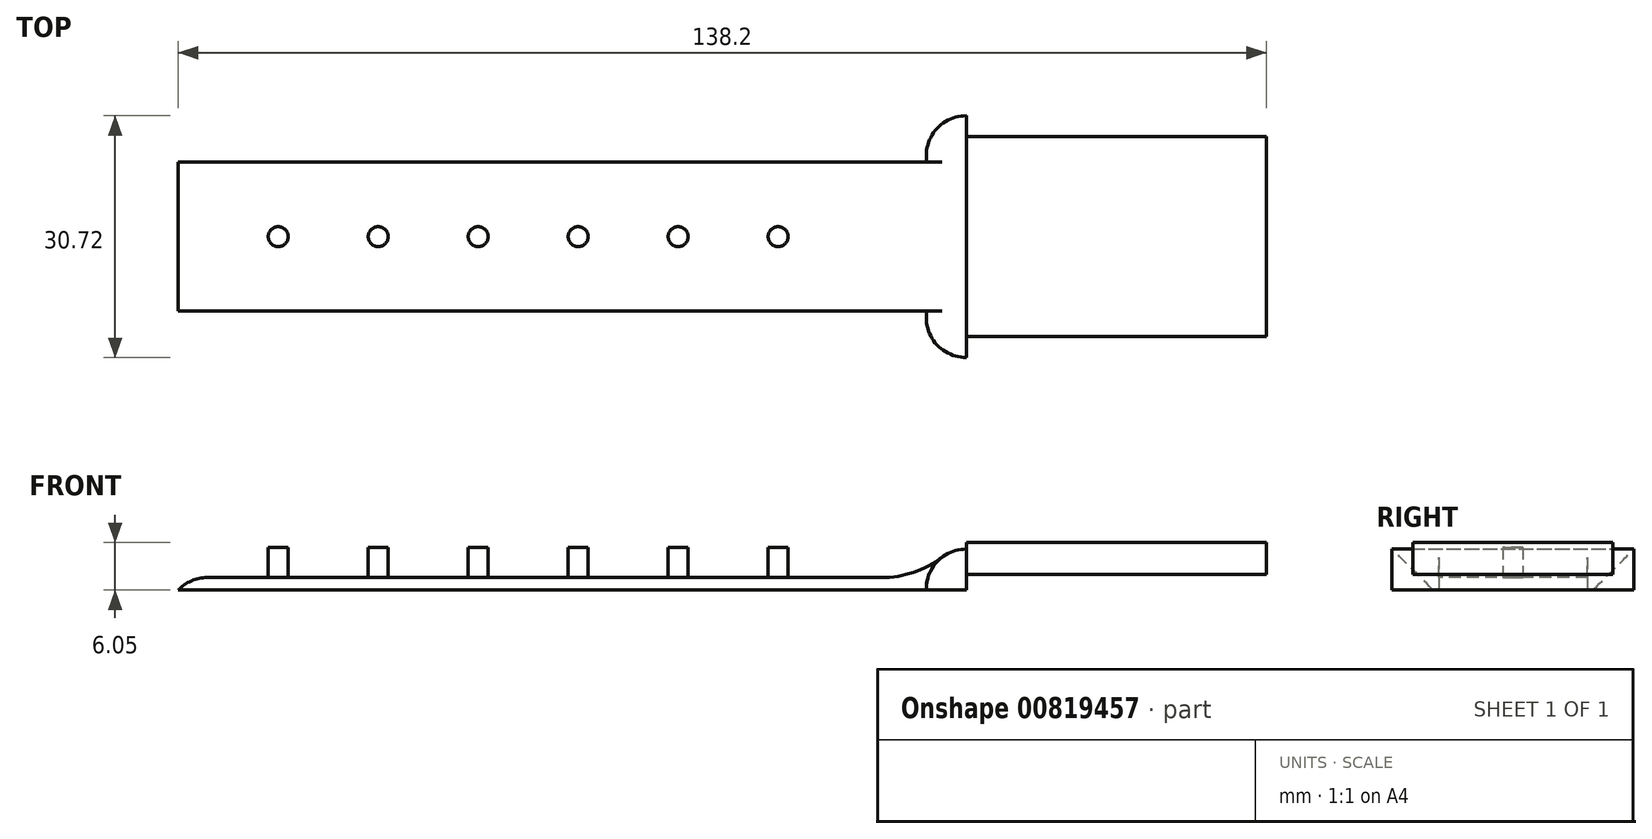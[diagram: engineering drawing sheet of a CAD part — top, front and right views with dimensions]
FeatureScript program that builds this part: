
annotation { "Feature Type Name" : "Feature", "Feature Type Description" : "" }
export const myFeature = defineFeature(function(context is Context, id is Id, definition is map)
    precondition{}
    {
        {
            var Q0;
            Q0=qCreatedBy(makeId("Top.planeOp"),FACE);
            var sketch = newSketch(context, id + "F0", { "sketchPlane" : qUnion([Q0])});
            skLineSegment(sketch, "E0.bottom", {"start": v(24.46, -15.36) * mm, "end": v(-24.46, -15.36) * mm});
            skLineSegment(sketch, "E0.top", {"start": v(24.46, 15.36) * mm, "end": v(-24.46, 15.36) * mm});
            skLineSegment(sketch, "E0.left", {"start": v(24.46, -15.36) * mm, "end": v(24.46, 15.36) * mm});
            skLineSegment(sketch, "E0.right", {"start": v(-24.46, -15.36) * mm, "end": v(-24.46, 15.36) * mm});
            skPoint(sketch, "E0.middle", {"position": v(0, 0) * mm});
            skLineSegment(sketch, "E1.bottom", {"start": v(-24.46, -9.45) * mm, "end": v(-119.48, -9.45) * mm});
            skLineSegment(sketch, "E1.top", {"start": v(-24.46, 9.45) * mm, "end": v(-119.48, 9.45) * mm});
            skLineSegment(sketch, "E1.left", {"start": v(-24.46, -9.45) * mm, "end": v(-24.46, 9.45) * mm});
            skLineSegment(sketch, "E1.right", {"start": v(-119.48, -9.45) * mm, "end": v(-119.48, 9.45) * mm});
            skLineSegment(sketch, "E2.MirrorCS", {"start": v(24.46, 9.45) * mm, "end": v(119.48, 9.45) * mm});
            skLineSegment(sketch, "E3.MirrorCS", {"start": v(119.48, -9.45) * mm, "end": v(119.48, 9.45) * mm});
            skLineSegment(sketch, "E4.MirrorCS", {"start": v(24.46, -9.45) * mm, "end": v(119.48, -9.45) * mm});
            skSolve(sketch);
        }
        {
            var Q0;
            Q0=qSketchRegion(id+"F0",true);
            extrude(context, id + "F1", {"entities" : qUnion([Q0]), "depth" : 1.6 * mm, "offsetDistance" : 25.4 * mm});
        }
        {
            var Q0;
            Q0=makeQuery(id+"F1.opExtrude","CAP_FACE",FACE,{"disambiguationData":[OSD([sQuery(id+"F0.wireOp",EDGE,"E0.bottom"),sQuery(id+"F0.wireOp",EDGE,"E0.top"),sQuery(id+"F0.wireOp",EDGE,"E0.left"),sQuery(id+"F0.wireOp",EDGE,"E0.right"),sQuery(id+"F0.wireOp",EDGE,"E1.bottom"),sQuery(id+"F0.wireOp",EDGE,"E1.top"),sQuery(id+"F0.wireOp",EDGE,"E1.right"),sQuery(id+"F0.wireOp",EDGE,"E2.MirrorCS"),sQuery(id+"F0.wireOp",EDGE,"E3.MirrorCS"),sQuery(id+"F0.wireOp",EDGE,"E4.MirrorCS")])],"isStart":false});
            var sketch = newSketch(context, id + "F2", { "sketchPlane" : qUnion([Q0])});
            skLineSegment(sketch, "E5", {"start": v(119.48, 0) * mm, "end": v(106.78, 0) * mm, "construction": true});
            skLineSegment(sketch, "E6", {"start": v(106.78, 0) * mm, "end": v(94.08, 0) * mm, "construction": true});
            skLineSegment(sketch, "E7", {"start": v(94.08, 0) * mm, "end": v(81.38, 0) * mm, "construction": true});
            skLineSegment(sketch, "E8", {"start": v(81.38, 0) * mm, "end": v(68.68, 0) * mm, "construction": true});
            skLineSegment(sketch, "E9", {"start": v(68.68, 0) * mm, "end": v(55.98, 0) * mm, "construction": true});
            skLineSegment(sketch, "E10", {"start": v(55.98, 0) * mm, "end": v(43.28, 0) * mm, "construction": true});
            skCircle(sketch, "E11", {"center": v(106.78, 0) * mm, "radius": 1.27 * mm});
            skCircle(sketch, "E12", {"center": v(94.08, 0) * mm, "radius": 1.27 * mm});
            skCircle(sketch, "E13", {"center": v(81.38, 0) * mm, "radius": 1.27 * mm});
            skCircle(sketch, "E14", {"center": v(68.68, 0) * mm, "radius": 1.27 * mm});
            skCircle(sketch, "E15", {"center": v(55.98, 0) * mm, "radius": 1.27 * mm});
            skCircle(sketch, "E16", {"center": v(43.28, 0) * mm, "radius": 1.27 * mm});
            skSolve(sketch);
        }
        {
            var Q0;
            Q0=qSketchRegion(id+"F2",true);
            extrude(context, id + "F3", {"entities" : qUnion([Q0]), "operationType" : NewBodyOperationType.REMOVE, "oppositeDirection" : true, "depth" : 25.4 * mm, "offsetDistance" : 25.4 * mm});
        }
        {
            var Q0;
            Q0=makeQuery(id+"F2.imprint","IMPRINT",FACE,{"disambiguationData":[TD([[makeQuery(id+"F2.imprint","IMPRINT",EDGE,{"derivedFrom":sQuery(id+"F2.wireOp",EDGE,"E11")}),-1.0]])]});
            var sketch = newSketch(context, id + "F4", { "sketchPlane" : qUnion([Q0])});
            skLineSegment(sketch, "E17", {"start": v(-119.47, 0) * mm, "end": v(-106.77, 0) * mm, "construction": true});
            skLineSegment(sketch, "E18", {"start": v(-106.77, 0) * mm, "end": v(-94.07, 0) * mm, "construction": true});
            skLineSegment(sketch, "E19", {"start": v(-94.07, 0) * mm, "end": v(-81.37, 0) * mm, "construction": true});
            skLineSegment(sketch, "E20", {"start": v(-81.37, 0) * mm, "end": v(-68.67, 0) * mm, "construction": true});
            skLineSegment(sketch, "E21", {"start": v(-68.67, 0) * mm, "end": v(-55.97, 0) * mm, "construction": true});
            skLineSegment(sketch, "E22", {"start": v(-55.97, 0) * mm, "end": v(-43.27, 0) * mm, "construction": true});
            skCircle(sketch, "E23", {"center": v(-106.77, 0) * mm, "radius": 1.27 * mm});
            skCircle(sketch, "E24", {"center": v(-94.07, 0) * mm, "radius": 1.27 * mm});
            skCircle(sketch, "E25", {"center": v(-81.37, 0) * mm, "radius": 1.27 * mm});
            skCircle(sketch, "E26", {"center": v(-68.67, 0) * mm, "radius": 1.27 * mm});
            skCircle(sketch, "E27", {"center": v(-55.97, 0) * mm, "radius": 1.27 * mm});
            skCircle(sketch, "E28", {"center": v(-43.27, 0) * mm, "radius": 1.27 * mm});
            skSolve(sketch);
        }
        {
            var Q0;
            Q0=qSketchRegion(id+"F4",true);
            extrude(context, id + "F5", {"entities" : qUnion([Q0]), "operationType" : NewBodyOperationType.ADD, "depth" : 3.8 * mm, "offsetDistance" : 25.4 * mm});
        }
        {
            var Q0;
            Q0=makeQuery(id+"F1.opExtrude","CAP_FACE",FACE,{"disambiguationData":[OSD([sQuery(id+"F0.wireOp",EDGE,"E0.bottom"),sQuery(id+"F0.wireOp",EDGE,"E0.top"),sQuery(id+"F0.wireOp",EDGE,"E0.left"),sQuery(id+"F0.wireOp",EDGE,"E0.right"),sQuery(id+"F0.wireOp",EDGE,"E1.bottom"),sQuery(id+"F0.wireOp",EDGE,"E1.top"),sQuery(id+"F0.wireOp",EDGE,"E1.right"),sQuery(id+"F0.wireOp",EDGE,"E2.MirrorCS"),sQuery(id+"F0.wireOp",EDGE,"E3.MirrorCS"),sQuery(id+"F0.wireOp",EDGE,"E4.MirrorCS")])],"isStart":false});
            var sketch = newSketch(context, id + "F6", { "sketchPlane" : qUnion([Q0])});
            skLineSegment(sketch, "E29.bottom", {"start": v(-24.46, 15.36) * mm, "end": v(24.46, 15.36) * mm});
            skLineSegment(sketch, "E29.top", {"start": v(-24.46, -15.36) * mm, "end": v(24.46, -15.36) * mm});
            skLineSegment(sketch, "E29.left", {"start": v(-24.46, 15.36) * mm, "end": v(-24.46, -15.36) * mm});
            skLineSegment(sketch, "E29.right", {"start": v(24.46, 15.36) * mm, "end": v(24.46, -15.36) * mm});
            skSolve(sketch);
        }
        {
            var Q0;
            Q0=qSketchRegion(id+"F6",true);
            extrude(context, id + "F7", {"entities" : qUnion([Q0]), "operationType" : NewBodyOperationType.ADD, "depth" : 3.62 * mm, "offsetDistance" : 25.4 * mm});
        }
        {
            var Q0;
            Q0=makeQuery(id+"F7.opExtrude","CAP_EDGE",EDGE,{"disambiguationData":[OSD([sQuery(id+"F6.wireOp",EDGE,"E29.right")])],"isStart":false});
            var Q1;
            Q1=makeQuery(id+"F7.opExtrude","CAP_EDGE",EDGE,{"disambiguationData":[OSD([sQuery(id+"F6.wireOp",EDGE,"E29.left")])],"isStart":false});
            var Q2;
            Q2=makeQuery(id+"F7.boolean.opBoolean","MERGE",EDGE,{"derivedFrom":[makeQuery(id+"F1.opExtrude","SWEPT_EDGE",EDGE,{"disambiguationData":[OSD([sQuery(id+"F0.wireOp",EDGE,"E0.top"),sQuery(id+"F0.wireOp",EDGE,"E0.right")])]}),makeQuery(id+"F7.opExtrude","SWEPT_EDGE",EDGE,{"disambiguationData":[OSD([sQuery(id+"F6.wireOp",EDGE,"E29.bottom"),sQuery(id+"F6.wireOp",EDGE,"E29.left")])]})]});
            var Q3;
            Q3=makeQuery(id+"F7.boolean.opBoolean","MERGE",EDGE,{"derivedFrom":[makeQuery(id+"F1.opExtrude","SWEPT_EDGE",EDGE,{"disambiguationData":[OSD([sQuery(id+"F0.wireOp",EDGE,"E0.bottom"),sQuery(id+"F0.wireOp",EDGE,"E0.right")])]}),makeQuery(id+"F7.opExtrude","SWEPT_EDGE",EDGE,{"disambiguationData":[OSD([sQuery(id+"F6.wireOp",EDGE,"E29.top"),sQuery(id+"F6.wireOp",EDGE,"E29.left")])]})]});
            var Q4;
            Q4=makeQuery(id+"F7.boolean.opBoolean","MERGE",EDGE,{"derivedFrom":[makeQuery(id+"F1.opExtrude","SWEPT_EDGE",EDGE,{"disambiguationData":[OSD([sQuery(id+"F0.wireOp",EDGE,"E0.bottom"),sQuery(id+"F0.wireOp",EDGE,"E0.left")])]}),makeQuery(id+"F7.opExtrude","SWEPT_EDGE",EDGE,{"disambiguationData":[OSD([sQuery(id+"F6.wireOp",EDGE,"E29.top"),sQuery(id+"F6.wireOp",EDGE,"E29.right")])]})]});
            var Q5;
            Q5=makeQuery(id+"F7.boolean.opBoolean","MERGE",EDGE,{"derivedFrom":[makeQuery(id+"F1.opExtrude","SWEPT_EDGE",EDGE,{"disambiguationData":[OSD([sQuery(id+"F0.wireOp",EDGE,"E0.top"),sQuery(id+"F0.wireOp",EDGE,"E0.left")])]}),makeQuery(id+"F7.opExtrude","SWEPT_EDGE",EDGE,{"disambiguationData":[OSD([sQuery(id+"F6.wireOp",EDGE,"E29.bottom"),sQuery(id+"F6.wireOp",EDGE,"E29.right")])]})]});
            fillet(context, id + "F8", {"entities" : qUnion([Q0, Q1, Q2, Q3, Q4, Q5]), "radius" : 5.08 * mm, "tangentPropagation" : true, "allowEdgeOverflow" : false});
        }
        {
            var Q0;
            Q0=makeQuery(id+"F1.opExtrude","CAP_EDGE",EDGE,{"disambiguationData":[OSD([sQuery(id+"F0.wireOp",EDGE,"E3.MirrorCS")])],"isStart":false});
            var Q1;
            Q1=makeQuery(id+"F1.opExtrude","CAP_EDGE",EDGE,{"disambiguationData":[OSD([sQuery(id+"F0.wireOp",EDGE,"E1.right")])],"isStart":false});
            fillet(context, id + "F9", {"entities" : qUnion([Q0, Q1]), "radius" : 5.08 * mm, "tangentPropagation" : true, "allowEdgeOverflow" : false});
        }
        {
            var Q0;
            {var subQ0=sQuery(id+"F0.wireOp",EDGE,"E4.MirrorCS");var subQ1=sQuery(id+"F0.wireOp",EDGE,"E0.left");var subQ2=sQuery(id+"F0.wireOp",EDGE,"E0.bottom");var subQ3=sQuery(id+"F0.wireOp",EDGE,"E0.top");var subQ4=sQuery(id+"F0.wireOp",EDGE,"E2.MirrorCS");var subQ5=sQuery(id+"F0.wireOp",EDGE,"E3.MirrorCS");var subQ6=sQuery(id+"F6.wireOp",EDGE,"E29.right");Q0=makeQuery(id+"F8.opFillet","BLEND_EDGE",EDGE,{"blendedFrom":[makeQuery(id+"F7.opExtrude","CAP_EDGE",EDGE,{"disambiguationData":[OSD([subQ6])],"isStart":false}),makeQuery(id+"F7.boolean.opBoolean","SPLIT",FACE,{"disambiguationData":[TD([makeQuery(id+"F1.opExtrude","SWEPT_FACE",FACE,{"disambiguationData":[OSD([subQ4])]})])],"derivedFrom":makeQuery(id+"F1.opExtrude","CAP_FACE",FACE,{"disambiguationData":[OSD([subQ2,subQ3,subQ1,sQuery(id+"F0.wireOp",EDGE,"E0.right"),sQuery(id+"F0.wireOp",EDGE,"E1.bottom"),sQuery(id+"F0.wireOp",EDGE,"E1.top"),sQuery(id+"F0.wireOp",EDGE,"E1.right"),subQ4,subQ5,subQ0])],"isStart":false})})],"blendedInto":[makeQuery(id+"F7.boolean.opBoolean","SPLIT",FACE,{"disambiguationData":[TD([makeQuery(id+"F1.opExtrude","SWEPT_FACE",FACE,{"disambiguationData":[OSD([subQ4])]})])],"derivedFrom":makeQuery(id+"F1.opExtrude","CAP_FACE",FACE,{"disambiguationData":[OSD([subQ2,subQ3,subQ1,sQuery(id+"F0.wireOp",EDGE,"E0.right"),sQuery(id+"F0.wireOp",EDGE,"E1.bottom"),sQuery(id+"F0.wireOp",EDGE,"E1.top"),sQuery(id+"F0.wireOp",EDGE,"E1.right"),subQ4,subQ5,subQ0])],"isStart":false})})]});}
            var Q1;
            {var subQ0=sQuery(id+"F0.wireOp",EDGE,"E1.right");var subQ1=sQuery(id+"F0.wireOp",EDGE,"E0.right");var subQ2=sQuery(id+"F0.wireOp",EDGE,"E0.bottom");var subQ4=sQuery(id+"F0.wireOp",EDGE,"E1.bottom");var subQ5=sQuery(id+"F0.wireOp",EDGE,"E0.top");var subQ6=sQuery(id+"F0.wireOp",EDGE,"E1.top");var subQ7=sQuery(id+"F6.wireOp",EDGE,"E29.left");Q1=makeQuery(id+"F8.opFillet","BLEND_EDGE",EDGE,{"blendedFrom":[makeQuery(id+"F7.opExtrude","CAP_EDGE",EDGE,{"disambiguationData":[OSD([subQ7])],"isStart":false}),makeQuery(id+"F7.boolean.opBoolean","SPLIT",FACE,{"disambiguationData":[TD([makeQuery(id+"F1.opExtrude","SWEPT_FACE",FACE,{"disambiguationData":[OSD([subQ4])]})])],"derivedFrom":makeQuery(id+"F1.opExtrude","CAP_FACE",FACE,{"disambiguationData":[OSD([subQ2,subQ5,sQuery(id+"F0.wireOp",EDGE,"E0.left"),subQ1,subQ4,subQ6,subQ0,sQuery(id+"F0.wireOp",EDGE,"E2.MirrorCS"),sQuery(id+"F0.wireOp",EDGE,"E3.MirrorCS"),sQuery(id+"F0.wireOp",EDGE,"E4.MirrorCS")])],"isStart":false})})],"blendedInto":[makeQuery(id+"F7.boolean.opBoolean","SPLIT",FACE,{"disambiguationData":[TD([makeQuery(id+"F1.opExtrude","SWEPT_FACE",FACE,{"disambiguationData":[OSD([subQ4])]})])],"derivedFrom":makeQuery(id+"F1.opExtrude","CAP_FACE",FACE,{"disambiguationData":[OSD([subQ2,subQ5,sQuery(id+"F0.wireOp",EDGE,"E0.left"),subQ1,subQ4,subQ6,subQ0,sQuery(id+"F0.wireOp",EDGE,"E2.MirrorCS"),sQuery(id+"F0.wireOp",EDGE,"E3.MirrorCS"),sQuery(id+"F0.wireOp",EDGE,"E4.MirrorCS")])],"isStart":false})})]});}
            fillet(context, id + "F10", {"entities" : qUnion([Q0, Q1]), "radius" : 12.7 * mm, "tangentPropagation" : true, "allowEdgeOverflow" : false});
        }
        {
            var Q0;
            Q0=qCreatedBy(makeId("Right.planeOp"),FACE);
            cPlane(context, id + "F11", {"entities" : qUnion([Q0]), "cplaneType" : CPlaneType.OFFSET, "offset" : 19.38 * mm, "oppositeDirection" : true, "width" : 152.4 * mm, "height" : 152.4 * mm});
        }
        {
            var Q0;
            Q0=qCreatedBy(id+"F11.planeOp",FACE);
            var sketch = newSketch(context, id + "F12", { "sketchPlane" : qUnion([Q0])});
            skCircle(sketch, "E30", {"center": v(0, 0) * mm, "radius": 39.98 * mm});
            skSolve(sketch);
        }
        {
            var Q0;
            Q0=makeQuery(id+"F12.imprint","IMPRINT",FACE,{"disambiguationData":[TD([[makeQuery(id+"F12.imprint","IMPRINT",EDGE,{"derivedFrom":sQuery(id+"F12.wireOp",EDGE,"E30")}),1.0]])]});
            extrude(context, id + "F13", {"entities" : qUnion([Q0]), "operationType" : NewBodyOperationType.REMOVE, "depth" : 162.56 * mm, "offsetDistance" : 25.4 * mm});
        }
        {
            var Q0;
            Q0=qCreatedBy(id+"F11.planeOp",FACE);
            var sketch = newSketch(context, id + "F14", { "sketchPlane" : qUnion([Q0])});
            skLineSegment(sketch, "E31", {"start": v(0, 0) * mm, "end": v(0, 4.01) * mm, "construction": true});
            skLineSegment(sketch, "E32.bottom", {"start": v(12.7, 1.98) * mm, "end": v(-12.7, 1.98) * mm});
            skLineSegment(sketch, "E32.top", {"start": v(12.7, 6.05) * mm, "end": v(-12.7, 6.05) * mm});
            skLineSegment(sketch, "E32.left", {"start": v(12.7, 1.98) * mm, "end": v(12.7, 6.05) * mm});
            skLineSegment(sketch, "E32.right", {"start": v(-12.7, 1.98) * mm, "end": v(-12.7, 6.05) * mm});
            skPoint(sketch, "E32.middle", {"position": v(0, 4.01) * mm});
            skSolve(sketch);
        }
        {
            var Q0;
            Q0=makeQuery(id+"F14.imprint","IMPRINT",FACE,{"disambiguationData":[TD([[makeQuery(id+"F14.imprint","IMPRINT",EDGE,{"derivedFrom":sQuery(id+"F14.wireOp",EDGE,"E32.bottom")}),-1.0]])]});
            extrude(context, id + "F15", {"entities" : qUnion([Q0]), "operationType" : NewBodyOperationType.ADD, "depth" : 38.1 * mm, "offsetDistance" : 25.4 * mm});
        }
    });
